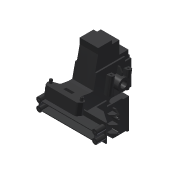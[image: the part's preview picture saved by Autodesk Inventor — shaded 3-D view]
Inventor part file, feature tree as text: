
AUTODESK INVENTOR PART (.ipt)
format: ipt  version: 2015 (Build 190159000, 159)  size: 589,312 bytes
history: native  units: in
note: dims shown in document units (in); Inventor stores cm internally (conversion verified against a paired STEP export)
features: extrude x15, sketch x15, mirror x5, plane x3, chamfer x2, other x1, projected_geometry x1
ambient origin geometry x8: Origin, YZ Plane, XZ Plane, XY Plane, X Axis, Y Axis, Z Axis, Center Point
bodies: Solid1 (feature_tree)
feature tree (42):
  extrude  "Extrusion1"  Depth=1.05in
  extrude  "Extrusion2"  Depth=1.15in
  extrude  "Extrusion3"  Depth=1.42in
  sketch  "Sketch4"  dims[d9=2.0in d10=0.43in]
  mirror  "Mirror1"
  extrude  "Extrusion4"  Depth=0.43in
  sketch  "Sketch5"  dims[d11=0.4in d12=0.97in]
  extrude  "Extrusion5"  Depth=0.97in
  extrude  "Extrusion6"  Depth=0.52in
  chamfer  "Chamfer1"  Distance=1.3in
  mirror  "Mirror2"
  extrude  "Extrusion7"  Depth=0.3in
  extrude  "Extrusion8"  Depth=0.43in
  chamfer  "Chamfer2"  Distance=0.1in
  extrude  "Extrusion9"  Depth=0.4in
  plane  "Work Plane2"
  mirror  "Mirror3"
  mirror  "Mirror4"
  plane  "Work Plane3"
  extrude  "Extrusion10"  Depth=0.372in
  extrude  "Extrusion11"  Depth=0.1in TaperAngle=0.0deg
  extrude  "Extrusion12"  Depth=0.1in TaperAngle=0.0deg
  extrude  "Extrusion13"  Depth=0.125in
  extrude  "Extrusion14"  Depth=0.125in
  mirror  "Mirror5"
  sketch  "Sketch15"  dims[d27=0.15in d28=0.3in d29=0.43in d30=0.1in d31=0.0in d32=0.4in d33=0.372in d34=0.1in d35=0.0in d36=0.1in d37=0.0in d38=0.125in d40=0.125in d41=0.4in d42=0.1in d43=0.0in d44=0.1in d47=0.1in d49=0.17in d51=0.24in d52=0.1in d53=0.32in d54=0.42in d55=0.51in d56=1.72in d57=0.76in d58=0.17in d59=0.98in d60=0.37in d61=0.426in d62=0.0in d63=0.25in d64=0.125in d65=45.0deg d67=0.82in d69=0.51in d70=0.65in d72=0.46in d73=0.54in d74=0.0in d75=0.0687in d76=0.382in d78=0.26in d79=1.15in d80=0.37in d81=0.1in d82=0.35in d83=0.0in d84=0.25in d85=0.125in d86=45.0deg d87=0.125in d89=0.35in d90=0.0in d92=0.0in d93=0.0687in d94=3.42in d95=90.0deg d96=0.58in d97=0.52in d99=0.69in d101=0.15in d102=0.34in d103=0.18in d104=0.125in d105=0.432in d106=0.238in d108=0.593in d109=0.767in d110=0.0in d111=0.194in d112=0.1in d113=0.215in d114=0.0in d115=4.314in d116=1.29in d117=0.08in d118=0.0in d120=0.5in d121=0.08in d122=0.0in d123=0.1in d124=0.1in d125=0.08in d126=0.0in d129=0.1875in d130=0.175in d131=0.175in d135=0.1875in d137=0.025in d138=0.025in d139=0.125in d140=0.609in d141=0.0in d142=1.0in d143=0.86in]
  plane  "Work Plane4"
  extrude  "Extrusion15"  Depth=0.4in
  sketch  "Sketch1"  dims[d0=2.128in d2=1.05in]
  sketch  "Sketch2"  dims[d3=1.08in d4=1.15in]
  sketch  "Sketch3"  dims[d5=0.55in d6=1.42in]
  sketch  "Sketch6"  dims[d13=0.25in d14=0.52in]
  sketch  "Sketch7"  dims[d15=0.9in]
  sketch  "Sketch8"  dims[d18=0.64in]
  sketch  "Sketch9"  dims[d19=0.37in]
  other  "Work Axis2"
  sketch  "Sketch10"  dims[d20=0.1in]
  sketch  "Sketch11"  dims[d21=1.9in]
  sketch  "Sketch12"  dims[d22=1.4in]
  sketch  "Sketch13"  dims[d23=0.29in]
  sketch  "Sketch14"  dims[d24=0.27in d25=1.3in d26=0.0in]
  projected_geometry  "Projected Loop1"
